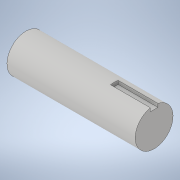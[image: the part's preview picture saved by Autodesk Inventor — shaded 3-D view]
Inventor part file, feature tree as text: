
AUTODESK INVENTOR PART (.ipt)
format: ipt  version: 2021 (Build 250183000, 183)  size: 105,472 bytes
history: native  units: in
note: dims shown in document units (in); Inventor stores cm internally (conversion verified against a paired STEP export)
features: extrude x2, sketch x2, plane x1
ambient origin geometry x8: Origin, YZ Plane, XZ Plane, XY Plane, X Axis, Y Axis, Z Axis, Center Point
bodies: Solid1 (feature_tree)
feature tree (5):
  extrude  "Extrusion1"  Depth=4.233in TaperAngle=0.0deg
  plane  "Work Plane1"
  extrude  "Extrusion9"  Depth=0.25in
  sketch  "Sketch1"  dims[d0=1.25in d1=4.233in d2=0.0in]
  sketch  "Sketch9"  dims[d11=-2.0535in d26=0.25in d27=0.125in d28=1.313in d29=0.0in]
